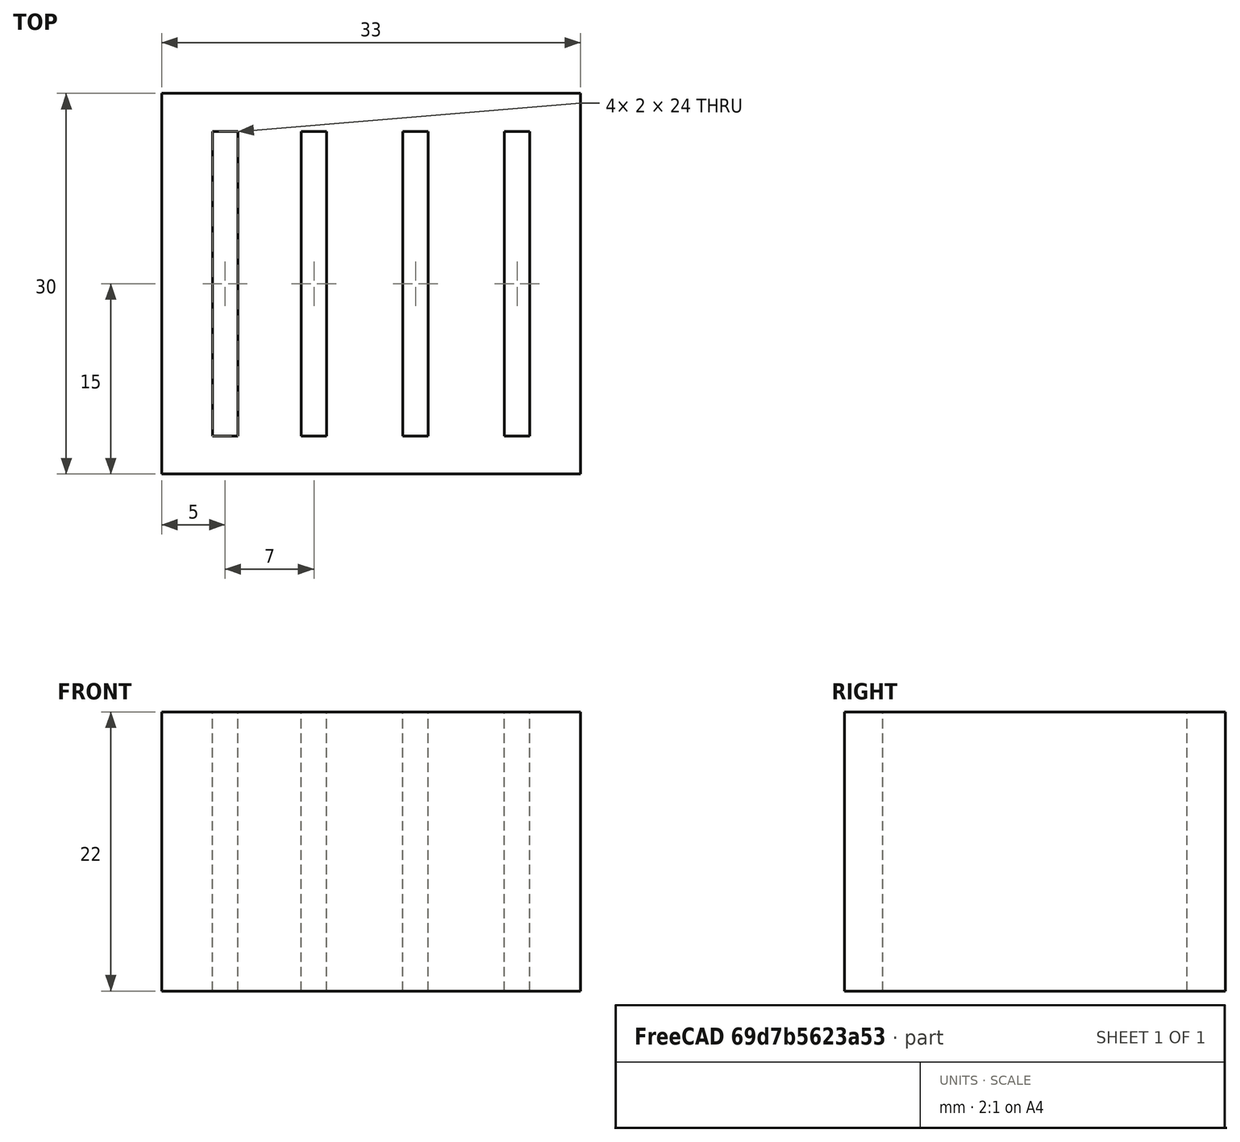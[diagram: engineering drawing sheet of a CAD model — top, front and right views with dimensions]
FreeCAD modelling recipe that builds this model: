
FCSTD DOCUMENT  (FreeCAD 1.0R39319 (Git))
Label: ojt1_t08r01_usb
License: All rights reserved
LicenseURL: https://en.wikipedia.org/wiki/All_rights_reserved
objects: Part::Box×5, Part::Cut×4
note: 9 computed .brp shape members not serialized (recipe doc carries the construction recipe); baked Part::Feature solids carry a one-line shape summary decoded from their .brp

FEATURE [Part::Box] Box  label="Cub"
  AttacherType = Attacher::AttachEngine3D
  Height = 22
  Length = 33
  Width = 30
FEATURE [Part::Box] Box001  label="Cub001"
  AttacherType = Attacher::AttachEngine3D
  Height = 25
  Length = 2
  Placement = pos=(4,3,-1) rot=(0,0,1;0rad)
  Width = 24
FEATURE [Part::Box] Box002  label="Cub002"
  AttacherType = Attacher::AttachEngine3D
  Height = 25
  Length = 2
  Placement = pos=(27,3,-1) rot=(0,0,1;0rad)
  Width = 24
FEATURE [Part::Box] Box003  label="Cub003"
  AttacherType = Attacher::AttachEngine3D
  Height = 25
  Length = 2
  Placement = pos=(19,3,-1) rot=(0,0,1;0rad)
  Width = 24
FEATURE [Part::Box] Box004  label="Cub004"
  AttacherType = Attacher::AttachEngine3D
  Height = 25
  Length = 2
  Placement = pos=(11,3,-1) rot=(0,0,1;0rad)
  Width = 24
FEATURE [Part::Cut] Cut
  Base = -> Box
  Refine = true
  Tool = -> Box001
FEATURE [Part::Cut] Cut001
  Base = -> Cut
  Refine = true
  Tool = -> Box004
FEATURE [Part::Cut] Cut002
  Base = -> Cut001
  Refine = true
  Tool = -> Box003
FEATURE [Part::Cut] Cut003
  Base = -> Cut002
  Refine = true
  Tool = -> Box002
